# Revit family: logis_single_lever_shower_mixer_for_exposed_installation_with_eco_ceramic_cartridge_71601000
name_source: partatom
category: Plumbing Fixtures
revit_build: Autodesk Revit 2015 (Build: 20140903_1530(x64)
units: mm (PartAtom-declared; Revit-internal decimal feet)

## types (1)
- Chrome 000
    BIMobject category = Taps & Mixers
    BOSUseNativeGeometries = 1
    Brand url = http://www.hansgrohe-int.com
    Default Elevation = 4' - 0"
    Design country = Germany
    EAN code = https://4011097737782
    Edition number = 1
    IFC Classification = Sanitary Terminal
    Installation instructions = https://pro.hansgrohe-int.com
    Manufacturer country = Germany
    Manufacturer name = hansgrohe
    Masterformat 2014 Code = 22 41 23
    Masterformat 2014 Description = Residential Showers
    Material main = Chrome
    NBS Reference Code = 35-06-82
    NBS Reference Description = Shower Mixers
    Nominal height = 0
    Nominal width = 0
    OmniClass Code = 23-31 15 11
    OmniClass Description = Bath Shower Units
    Product Guid = b5136a33-a6d1-4348-9d0d-b2f848f3786d
    Product SKU = 71601000
    Product data url = https://bimobject.com
    Product family = Logis
    Product group = Shower mixers
    Product name = Logis Single lever shower mixer for exposed installation with Eco ceramic cartridge 71601000
    Product url = https://pro.hansgrohe-int.com
    QR code = http://bimobject.com
    Technical description = https://pro.hansgrohe-int.com
    UNSPSC Code = 301815
    Uniclass 1.4 Code = L7214
    Uniclass 1.4 Description = Showers
    Uniclass 2.0 Code = PR-35-06-82
    Uniclass 2.0 Description = Shower Mixers
    Uniclass 2015 Code = Pr_60_75_08_54
    Uniclass 2015 Name = Mixers
    Uniformat II Code = D2090
    Uniformat II Description = Other Plumbing Systems
    Weight Net (Kg) = 0

## geometry (parser evidence)
native form markers: Sweep x2
no freeform markers — native parametric forms only
